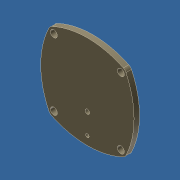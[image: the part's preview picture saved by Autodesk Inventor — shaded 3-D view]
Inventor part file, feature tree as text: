
AUTODESK INVENTOR PART (.ipt)
format: ipt  version: unknown  size: 249,344 bytes
history: native  units: in
note: dims shown in document units (in); Inventor stores cm internally (conversion verified against a paired STEP export)
features: extrude x3, sketch x2, revolve x1, reference x1
ambient origin geometry x8: Origin, YZ Plane, XZ Plane, XY Plane, X Axis, Y Axis, Z Axis, Center Point
bodies: Solid1 (feature_tree)
feature tree (7):
  extrude  "Extrusion1"  Depth=0.075in
  sketch  "Sketch2"  dims[d11=1.4in d13=0.1in d14=0.0in d15=0.1625in d16=0.1in d17=0.0in d18=0.125in d19=0.75in d21=0.675in d22=0.35in d23=90.0deg d36=0.25in d37=2.425in d38=2.425in d39=3.375in d40=0.1in d41=0.1in d42=0.1in d43=0.1in d44=2.6693in d45=2.6693in d46=0.425in d47=0.25in]
  extrude  "Extrusion2"  Depth=0.1in TaperAngle=0.0deg
  extrude  "Extrusion3"  Depth=0.1625in
  revolve  "Revolution1"  [1 undecoded]
  sketch  "Sketch1"  dims[d7=0.2in d8=0.0in d10=0.075in]
  reference  "Reference1"
note: 1 required parameter value undecoded (feature->parameter linkage not recoverable at this tier; creation-order binding heuristic only, values carry confidence <= 0.55)
